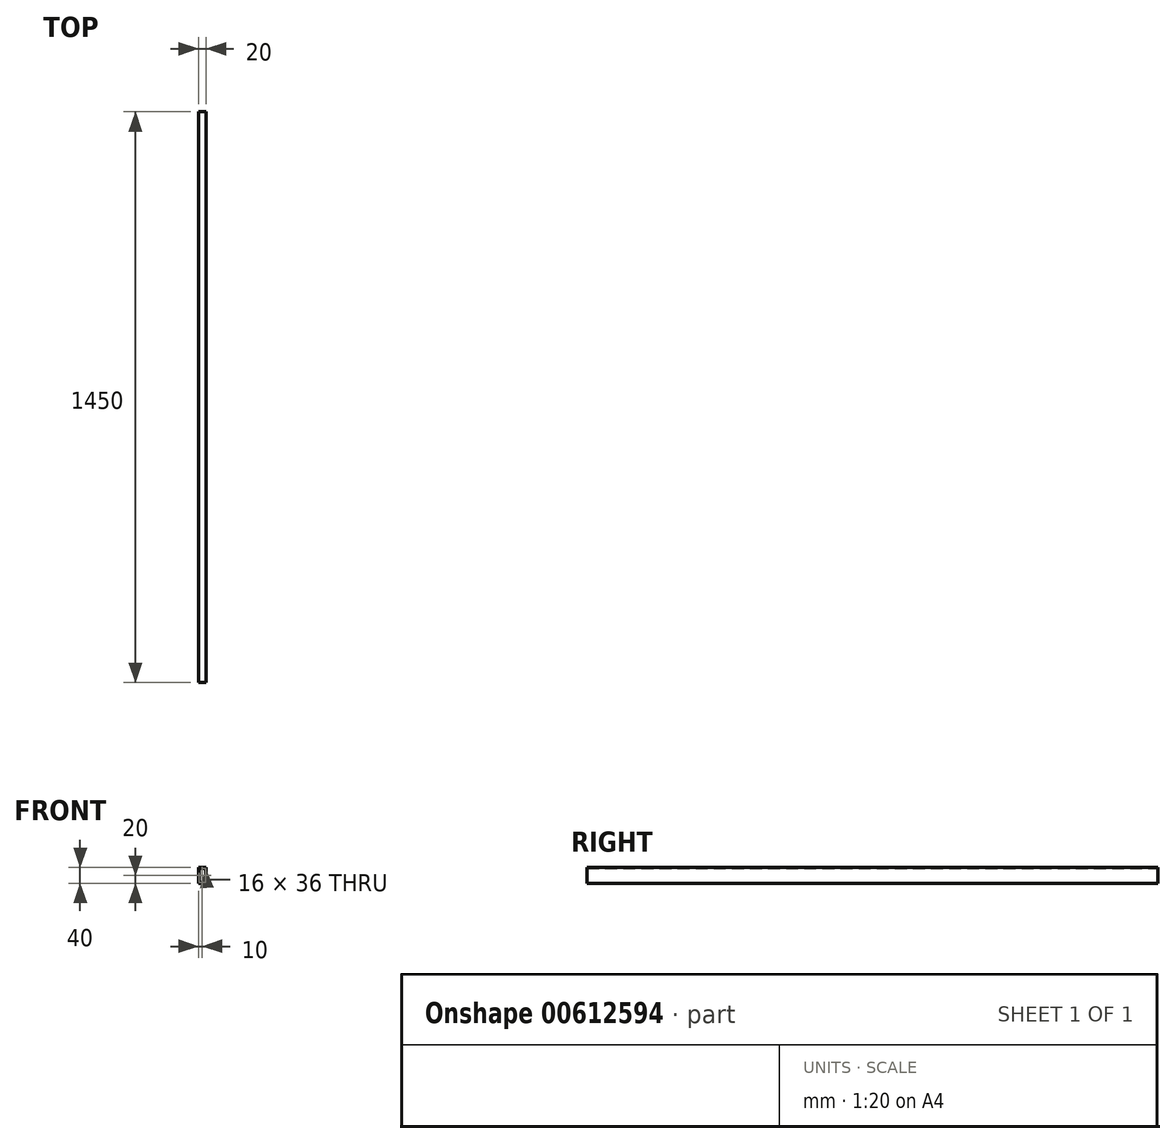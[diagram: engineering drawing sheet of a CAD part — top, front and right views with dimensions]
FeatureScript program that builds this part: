
annotation { "Feature Type Name" : "Feature", "Feature Type Description" : "" }
export const myFeature = defineFeature(function(context is Context, id is Id, definition is map)
    precondition{}
    {
        {
            var Q0;
            Q0=qCreatedBy(makeId("Front.planeOp"),FACE);
            var sketch = newSketch(context, id + "F0", { "sketchPlane" : qUnion([Q0])});
            skLineSegment(sketch, "E0.bottom", {"start": v(0, 0) * mm, "end": v(20, 0) * mm});
            skLineSegment(sketch, "E0.top", {"start": v(0, -40) * mm, "end": v(20, -40) * mm});
            skLineSegment(sketch, "E0.left", {"start": v(0, 0) * mm, "end": v(0, -40) * mm});
            skLineSegment(sketch, "E0.right", {"start": v(20, 0) * mm, "end": v(20, -40) * mm});
            skLineSegment(sketch, "E1.0", {"start": v(2, -2) * mm, "end": v(18, -2) * mm});
            skLineSegment(sketch, "E1.1", {"start": v(2, -2) * mm, "end": v(2, -38) * mm});
            skLineSegment(sketch, "E1.2", {"start": v(2, -38) * mm, "end": v(18, -38) * mm});
            skLineSegment(sketch, "E1.3", {"start": v(18, -2) * mm, "end": v(18, -38) * mm});
            skSolve(sketch);
        }
        {
            var Q0;
            Q0=makeQuery(id+"F0.imprint","IMPRINT",FACE,{"disambiguationData":[TD([[makeQuery(id+"F0.imprint","IMPRINT",EDGE,{"derivedFrom":sQuery(id+"F0.wireOp",EDGE,"E0.bottom")}),-1.0]])]});
            extrude(context, id + "F1", {"entities" : qUnion([Q0]), "depth" : 1450 * mm, "offsetDistance" : 25.4 * mm});
        }
    });
